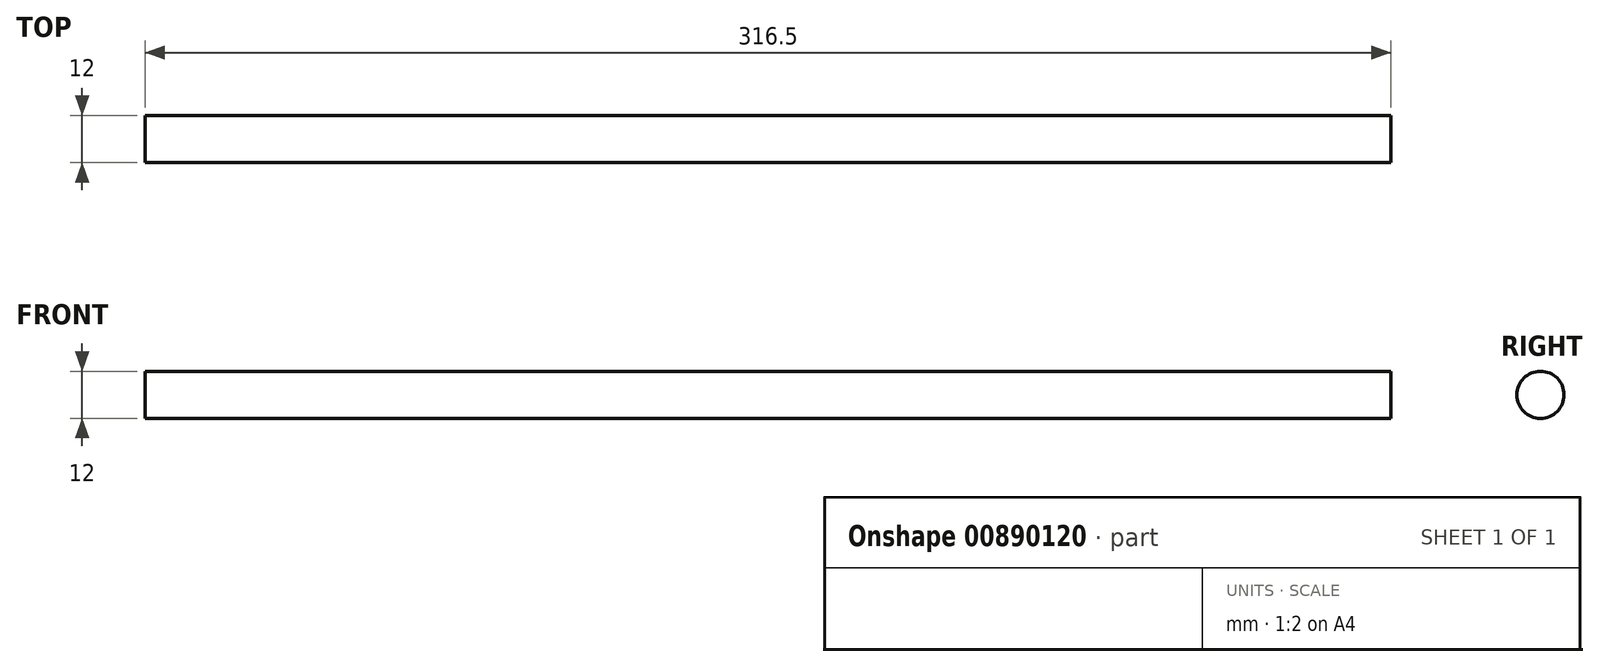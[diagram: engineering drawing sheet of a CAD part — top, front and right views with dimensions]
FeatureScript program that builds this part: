
annotation { "Feature Type Name" : "Feature", "Feature Type Description" : "" }
export const myFeature = defineFeature(function(context is Context, id is Id, definition is map)
    precondition{}
    {
        {
            var Q0;
            Q0=qCreatedBy(makeId("Right.planeOp"),FACE);
            var sketch = newSketch(context, id + "F0", { "sketchPlane" : qUnion([Q0])});
            skCircle(sketch, "E0", {"center": v(0, 0) * mm, "radius": 6 * mm});
            skSolve(sketch);
        }
        {
            var Q0;
            Q0=qSketchRegion(id+"F0",true);
            extrude(context, id + "F1", {"entities" : qUnion([Q0]), "depth" : 316.5 * mm, "offsetDistance" : 25 * mm});
        }
    });
